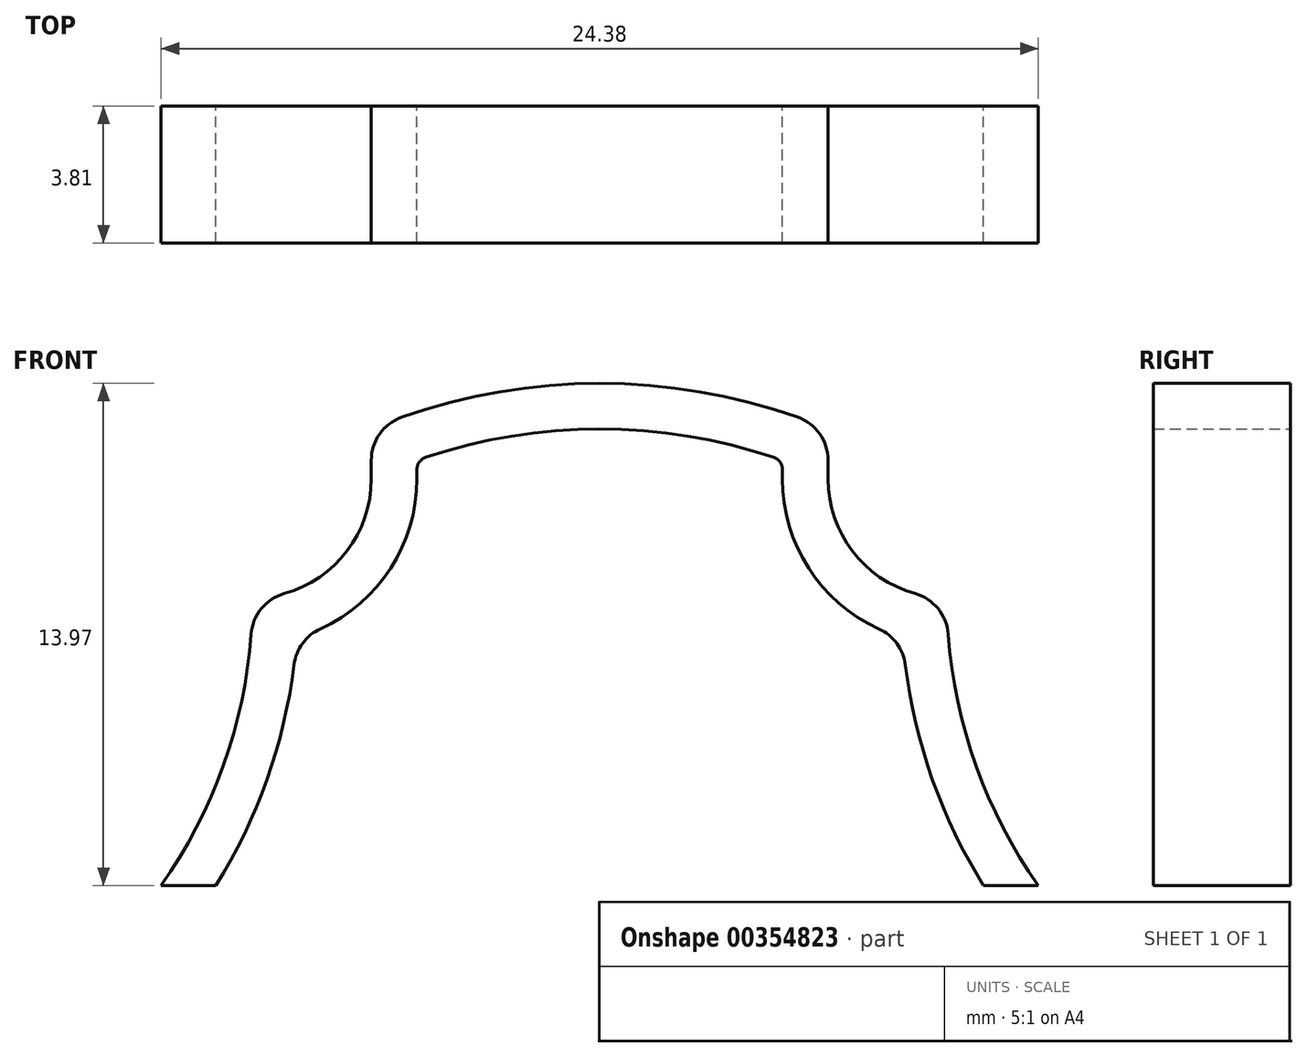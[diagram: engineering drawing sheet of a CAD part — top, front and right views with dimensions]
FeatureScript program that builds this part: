
annotation { "Feature Type Name" : "Feature", "Feature Type Description" : "" }
export const myFeature = defineFeature(function(context is Context, id is Id, definition is map)
    precondition{}
    {
        {
            var Q0;
            Q0=qCreatedBy(makeId("Front.planeOp"),FACE);
            var sketch = newSketch(context, id + "F0", { "sketchPlane" : qUnion([Q0])});
            skLineSegment(sketch, "E0.bottom", {"start": v(0, 0) * mm, "end": v(6.35, 0) * mm});
            skLineSegment(sketch, "E0.left", {"start": v(0, 0) * mm, "end": v(0, 12.7) * mm});
            skLineSegment(sketch, "E0.right", {"start": v(6.35, 11.3) * mm, "end": v(6.35, 11.83) * mm});
            skLineSegment(sketch, "E1", {"start": v(0, 12.7) * mm, "end": v(0, 13.97) * mm});
            skArc(sketch, "E2", {"start": v(5.5, 13.03) * mm, "mid": v(2.8, 13.73) * mm, "end": v(0, 13.97) * mm});
            skLineSegment(sketch, "E3", {"start": v(0, 13.97) * mm, "end": v(-8.02, 13.97) * mm});
            skLineSegment(sketch, "E4", {"start": v(6.35, 11.83) * mm, "end": v(6.35, 11.3) * mm});
            skLineSegment(sketch, "E5", {"start": v(9.65, 8) * mm, "end": v(9.65, 11.3) * mm});
            skArc(sketch, "E6", {"start": v(6.35, 11.3) * mm, "mid": v(7.02, 9.3) * mm, "end": v(8.76, 8.12) * mm});
            skLineSegment(sketch, "E7", {"start": v(6.35, 0) * mm, "end": v(9.65, 0) * mm});
            skPoint(sketch, "E8.orphan", {"position": v(12.86, 0) * mm});
            skLineSegment(sketch, "E9", {"start": v(9.65, 0) * mm, "end": v(12.2, 0) * mm});
            skArc(sketch, "E10", {"start": v(9.69, 7) * mm, "mid": v(10.46, 3.33) * mm, "end": v(12.2, 0) * mm});
            skPoint(sketch, "E11.visualSharp", {"position": v(9.65, 8) * mm});
            skArc(sketch, "E11.filletArc", {"start": v(9.69, 7) * mm, "mid": v(9.4, 7.7) * mm, "end": v(8.76, 8.12) * mm});
            skPoint(sketch, "E12.visualSharp", {"position": v(6.35, 12.7) * mm});
            skArc(sketch, "E12.filletArc", {"start": v(6.35, 11.83) * mm, "mid": v(6.12, 12.56) * mm, "end": v(5.5, 13.03) * mm});
            skArc(sketch, "E13.0", {"start": v(4.84, 11.91) * mm, "mid": v(2.45, 12.5) * mm, "end": v(0, 12.7) * mm});
            skLineSegment(sketch, "E13.1", {"start": v(5.08, 11.83) * mm, "end": v(5.08, 11.83) * mm});
            skArc(sketch, "E13.2", {"start": v(8.5, 6.14) * mm, "mid": v(9.25, 2.95) * mm, "end": v(10.67, 0) * mm});
            skLineSegment(sketch, "E13.3", {"start": v(8.42, 6.9) * mm, "end": v(8.42, 6.9) * mm});
            skArc(sketch, "E13.4", {"start": v(5.08, 11.3) * mm, "mid": v(5.8, 8.83) * mm, "end": v(7.76, 7.14) * mm});
            skLineSegment(sketch, "E13.5", {"start": v(5.08, 11.57) * mm, "end": v(5.08, 11.3) * mm});
            skArc(sketch, "E14.filletArc", {"start": v(8.5, 6.14) * mm, "mid": v(8.26, 6.74) * mm, "end": v(7.76, 7.14) * mm});
            skArc(sketch, "E15.filletArc", {"start": v(5.08, 11.57) * mm, "mid": v(5.01, 11.78) * mm, "end": v(4.84, 11.91) * mm});
            skArc(sketch, "E16.MirrorCS", {"start": v(-5.08, 11.57) * mm, "mid": v(-5.01, 11.78) * mm, "end": v(-4.84, 11.91) * mm});
            skLineSegment(sketch, "E17.MirrorCS", {"start": v(-5.08, 11.57) * mm, "end": v(-5.08, 11.3) * mm});
            skLineSegment(sketch, "E18.MirrorCS", {"start": v(-6.35, 11.3) * mm, "end": v(-6.35, 11.83) * mm});
            skLineSegment(sketch, "E19.MirrorCS", {"start": v(-6.35, 11.83) * mm, "end": v(-6.35, 11.3) * mm});
            skPoint(sketch, "E20.MirrorP", {"position": v(-5.08, 11.83) * mm});
            skArc(sketch, "E21.MirrorCS", {"start": v(-9.69, 7) * mm, "mid": v(-9.4, 7.7) * mm, "end": v(-8.76, 8.12) * mm});
            skArc(sketch, "E22.MirrorCS", {"start": v(-8.5, 6.14) * mm, "mid": v(-8.26, 6.74) * mm, "end": v(-7.76, 7.14) * mm});
            skLineSegment(sketch, "E23.MirrorCS", {"start": v(-5.08, 11.83) * mm, "end": v(-5.08, 11.83) * mm});
            skArc(sketch, "E24.MirrorCS", {"start": v(-6.35, 11.83) * mm, "mid": v(-6.12, 12.56) * mm, "end": v(-5.5, 13.03) * mm});
            skArc(sketch, "E25.MirrorCS", {"start": v(-5.08, 11.3) * mm, "mid": v(-5.8, 8.83) * mm, "end": v(-7.76, 7.14) * mm});
            skArc(sketch, "E26.MirrorCS", {"start": v(-9.69, 7) * mm, "mid": v(-10.46, 3.33) * mm, "end": v(-12.2, 0) * mm});
            skLineSegment(sketch, "E27.MirrorCS", {"start": v(-9.65, 0) * mm, "end": v(-12.2, 0) * mm});
            skLineSegment(sketch, "E28.MirrorCS", {"start": v(-6.35, 0) * mm, "end": v(-9.65, 0) * mm});
            skArc(sketch, "E29.MirrorCS", {"start": v(-6.35, 11.3) * mm, "mid": v(-7.02, 9.3) * mm, "end": v(-8.76, 8.12) * mm});
            skLineSegment(sketch, "E30.MirrorCS", {"start": v(-9.65, 8) * mm, "end": v(-9.65, 11.3) * mm});
            skPoint(sketch, "E31.MirrorP", {"position": v(-6.35, 12.7) * mm});
            skArc(sketch, "E32.MirrorCS", {"start": v(-4.84, 11.91) * mm, "mid": v(-2.45, 12.5) * mm, "end": v(0, 12.7) * mm});
            skPoint(sketch, "E33.MirrorP", {"position": v(-12.86, 0) * mm});
            skLineSegment(sketch, "E34.MirrorCS", {"start": v(-8.42, 6.9) * mm, "end": v(-8.42, 6.9) * mm});
            skArc(sketch, "E35.MirrorCS", {"start": v(-5.5, 13.03) * mm, "mid": v(-2.8, 13.73) * mm, "end": v(0, 13.97) * mm});
            skArc(sketch, "E36.MirrorCS", {"start": v(-8.5, 6.14) * mm, "mid": v(-9.25, 2.95) * mm, "end": v(-10.67, 0) * mm});
            skPoint(sketch, "E37.MirrorP", {"position": v(-9.65, 8) * mm});
            skLineSegment(sketch, "E38.MirrorCS", {"start": v(0, 0) * mm, "end": v(-6.35, 0) * mm});
            skSolve(sketch);
        }
        {
            var Q0;
            Q0=makeQuery(id+"F0.imprint","IMPRINT",FACE,{"disambiguationData":[TD([[makeQuery(id+"F0.imprint","IMPRINT",EDGE,{"derivedFrom":sQuery(id+"F0.wireOp",EDGE,"E1")}),-1.0]])]});
            var Q1;
            Q1=makeQuery(id+"F0.imprint","IMPRINT",FACE,{"disambiguationData":[TD([[makeQuery(id+"F0.imprint","IMPRINT",EDGE,{"derivedFrom":sQuery(id+"F0.wireOp",EDGE,"E1")}),1.0]])]});
            extrude(context, id + "F1", {"entities" : qUnion([Q0, Q1]), "depth" : 3.8 * mm});
        }
    });
